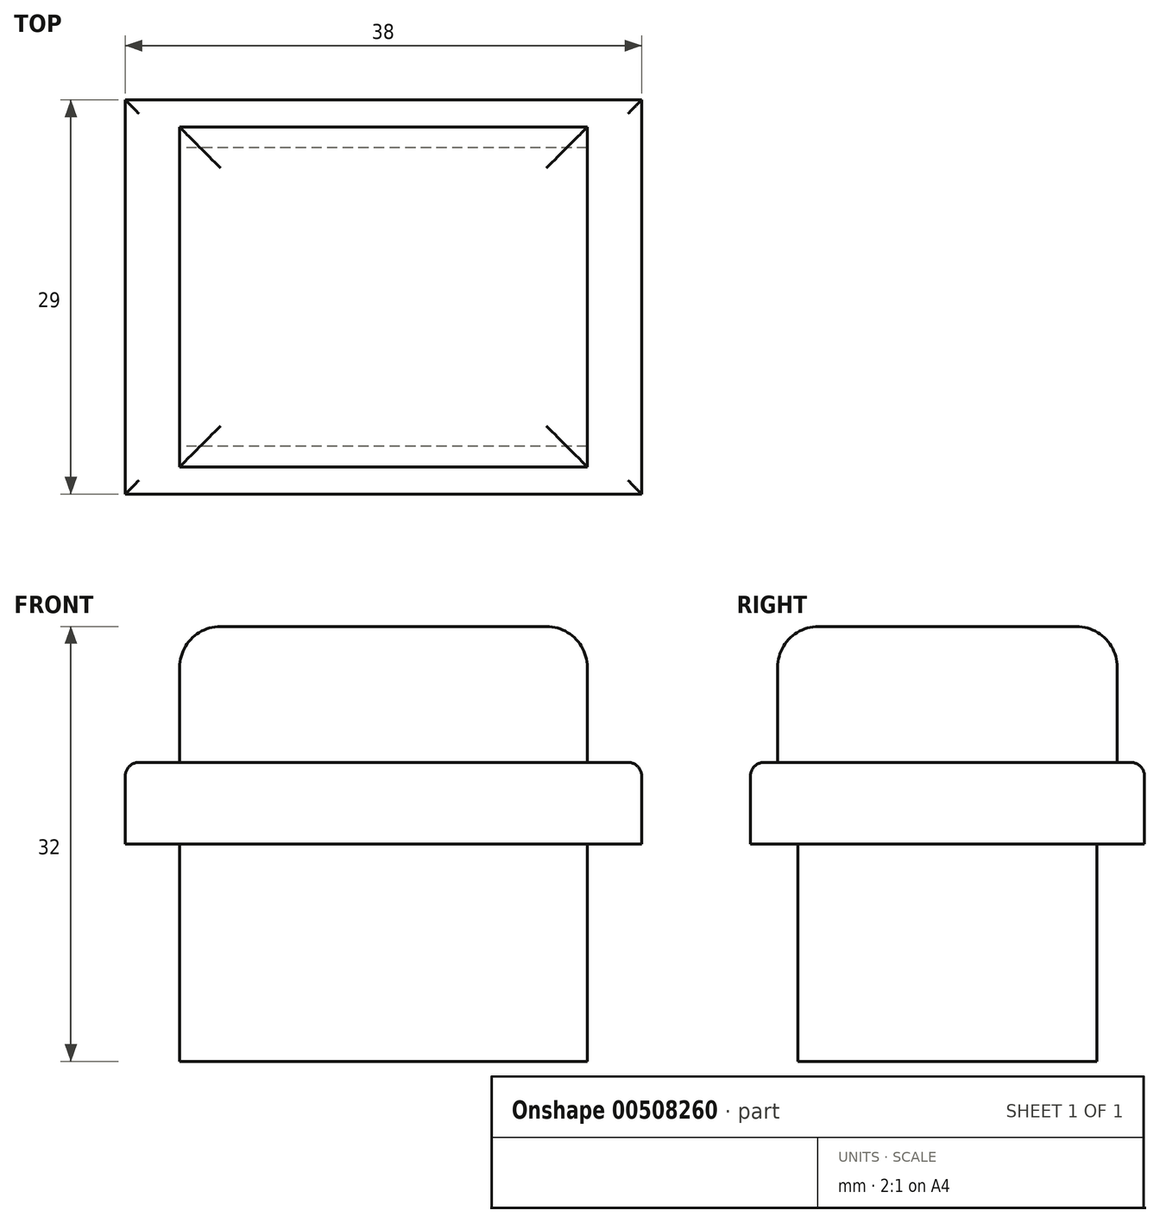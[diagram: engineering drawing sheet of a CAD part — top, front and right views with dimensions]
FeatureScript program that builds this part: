
annotation { "Feature Type Name" : "Feature", "Feature Type Description" : "" }
export const myFeature = defineFeature(function(context is Context, id is Id, definition is map)
    precondition{}
    {
        {
            var Q0;
            Q0=qCreatedBy(makeId("Top.planeOp"),FACE);
            var sketch = newSketch(context, id + "F0", { "sketchPlane" : qUnion([Q0])});
            skLineSegment(sketch, "E0.bottom", {"start": v(15, 11) * mm, "end": v(-15, 11) * mm});
            skLineSegment(sketch, "E0.top", {"start": v(15, -11) * mm, "end": v(-15, -11) * mm});
            skLineSegment(sketch, "E0.left", {"start": v(15, 11) * mm, "end": v(15, -11) * mm});
            skLineSegment(sketch, "E0.right", {"start": v(-15, 11) * mm, "end": v(-15, -11) * mm});
            skPoint(sketch, "E0.middle", {"position": v(0, 0) * mm});
            skSolve(sketch);
        }
        {
            var Q0;
            Q0=makeQuery(id+"F0.imprint","IMPRINT",FACE,{"disambiguationData":[TD([[makeQuery(id+"F0.imprint","IMPRINT",EDGE,{"derivedFrom":sQuery(id+"F0.wireOp",EDGE,"E0.bottom")}),1.0]])]});
            extrude(context, id + "F1", {"entities" : qUnion([Q0]), "depth" : 16 * mm});
        }
        {
            var Q0;
            Q0=makeQuery(id+"F1.opExtrude","CAP_FACE",FACE,{"disambiguationData":[OSD([sQuery(id+"F0.wireOp",EDGE,"E0.bottom"),sQuery(id+"F0.wireOp",EDGE,"E0.top"),sQuery(id+"F0.wireOp",EDGE,"E0.left"),sQuery(id+"F0.wireOp",EDGE,"E0.right")])],"isStart":false});
            var sketch = newSketch(context, id + "F2", { "sketchPlane" : qUnion([Q0])});
            skLineSegment(sketch, "E1.bottom", {"start": v(19, 14.5) * mm, "end": v(-19, 14.5) * mm});
            skLineSegment(sketch, "E1.top", {"start": v(19, -14.5) * mm, "end": v(-19, -14.5) * mm});
            skLineSegment(sketch, "E1.left", {"start": v(19, 14.5) * mm, "end": v(19, -14.5) * mm});
            skLineSegment(sketch, "E1.right", {"start": v(-19, 14.5) * mm, "end": v(-19, -14.5) * mm});
            skPoint(sketch, "E1.middle", {"position": v(0, 0) * mm});
            skSolve(sketch);
        }
        {
            var Q0;
            Q0=makeQuery(id+"F2.imprint","IMPRINT",FACE,{"disambiguationData":[TD([[makeQuery(id+"F2.imprint","IMPRINT",EDGE,{"derivedFrom":makeQuery(id+"F1.opExtrude","CAP_EDGE",EDGE,{"disambiguationData":[OSD([sQuery(id+"F0.wireOp",EDGE,"E0.bottom")])],"isStart":false})}),1.0]])]});
            var Q1;
            Q1=makeQuery(id+"F2.imprint","IMPRINT",FACE,{"disambiguationData":[TD([[makeQuery(id+"F2.imprint","IMPRINT",EDGE,{"derivedFrom":sQuery(id+"F2.wireOp",EDGE,"E1.bottom")}),1.0]])]});
            extrude(context, id + "F3", {"entities" : qUnion([Q0, Q1]), "operationType" : NewBodyOperationType.ADD, "depth" : 6 * mm});
        }
        {
            var Q0;
            Q0=makeQuery(id+"F3.opExtrude","CAP_FACE",FACE,{"disambiguationData":[OSD([sQuery(id+"F2.wireOp",EDGE,"E1.bottom"),sQuery(id+"F2.wireOp",EDGE,"E1.top"),sQuery(id+"F2.wireOp",EDGE,"E1.left"),sQuery(id+"F2.wireOp",EDGE,"E1.right")])],"isStart":false});
            fillet(context, id + "F4", {"entities" : qUnion([Q0]), "radius" : 1 * mm, "tangentPropagation" : true, "allowEdgeOverflow" : false});
        }
        {
            var Q0;
            Q0=qCreatedBy(makeId("Front.planeOp"),FACE);
            var sketch = newSketch(context, id + "F5", { "sketchPlane" : qUnion([Q0])});
            skLineSegment(sketch, "E2.0", {"start": v(-18, 22) * mm, "end": v(18, 22) * mm});
            skLineSegment(sketch, "E3", {"start": v(-15, 22) * mm, "end": v(-15, 32) * mm});
            skLineSegment(sketch, "E4", {"start": v(-15, 32) * mm, "end": v(15, 32) * mm});
            skLineSegment(sketch, "E5", {"start": v(15, 32) * mm, "end": v(15, 22) * mm});
            skLineSegment(sketch, "E6", {"start": v(0, 0) * mm, "end": v(0, 10.4) * mm, "construction": true});
            skSolve(sketch);
        }
        {
            var Q0;
            {var subQ0=sQuery(id+"F5.wireOp",EDGE,"E3");Q0=makeQuery(id+"F5.imprint","IMPRINT",FACE,{"disambiguationData":[TD([[makeQuery(id+"F5.imprint","IMPRINT",EDGE,{"derivedFrom":subQ0}),-1.0]])]});}
            extrude(context, id + "F6", {"entities" : qUnion([Q0]), "operationType" : NewBodyOperationType.ADD, "endBound" : BoundingType.SYMMETRIC, "depth" : 25 * mm});
        }
        {
            var Q0;
            Q0=makeQuery(id+"F6.opExtrude","SWEPT_FACE",FACE,{"disambiguationData":[OSD([sQuery(id+"F5.wireOp",EDGE,"E4")])]});
            fillet(context, id + "F7", {"entities" : qUnion([Q0]), "radius" : 3 * mm, "tangentPropagation" : true, "allowEdgeOverflow" : false});
        }
    });
